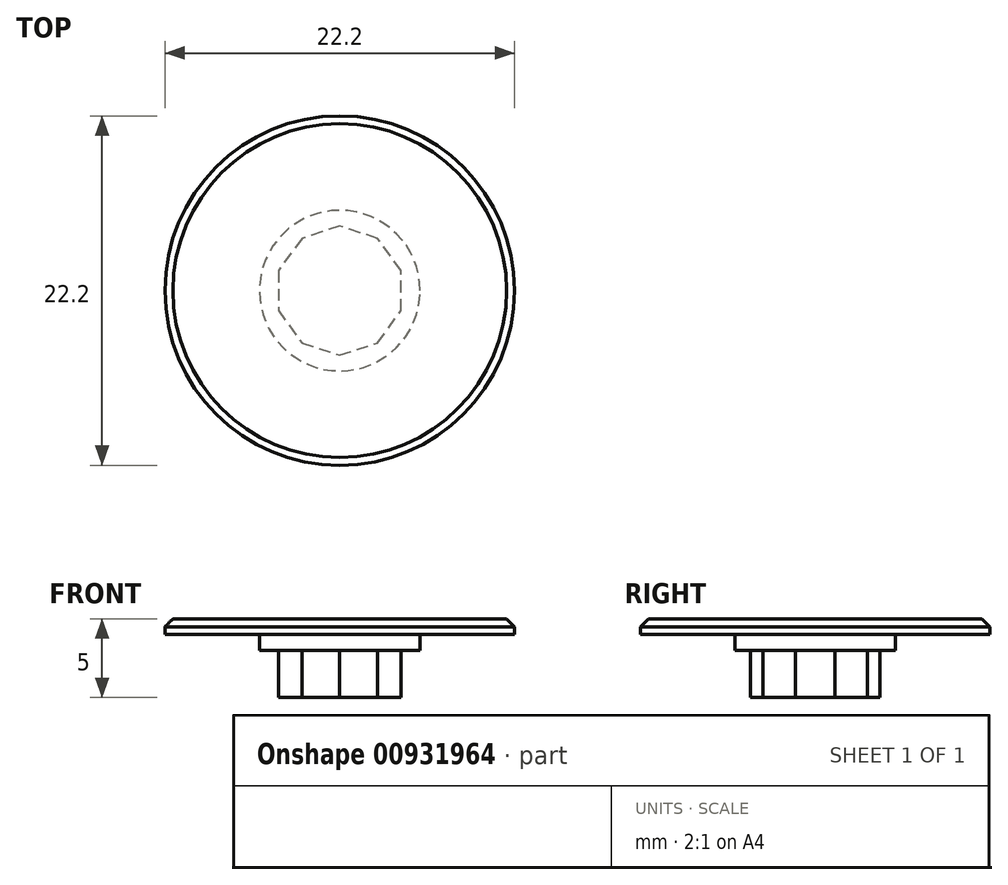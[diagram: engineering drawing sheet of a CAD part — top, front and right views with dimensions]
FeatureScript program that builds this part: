
annotation { "Feature Type Name" : "Feature", "Feature Type Description" : "" }
export const myFeature = defineFeature(function(context is Context, id is Id, definition is map)
    precondition{}
    {
        {
            var Q0;
            Q0=qCreatedBy(makeId("Front.planeOp"),FACE);
            var sketch = newSketch(context, id + "F0", { "sketchPlane" : qUnion([Q0])});
            skLineSegment(sketch, "E0", {"start": v(0, 0) * mm, "end": v(-4.1, 0) * mm});
            skLineSegment(sketch, "E1", {"start": v(-4.1, 0) * mm, "end": v(-4.1, 3) * mm});
            skLineSegment(sketch, "E2", {"start": v(-4.1, 3) * mm, "end": v(-5.1, 3) * mm});
            skLineSegment(sketch, "E3", {"start": v(0, 5) * mm, "end": v(0, 0) * mm});
            skLineSegment(sketch, "E4", {"start": v(-5.1, 3) * mm, "end": v(-5.1, 4) * mm});
            skLineSegment(sketch, "E5", {"start": v(-5.1, 4) * mm, "end": v(-11.1, 4) * mm});
            skLineSegment(sketch, "E6", {"start": v(-11.1, 4) * mm, "end": v(-11.1, 5) * mm});
            skLineSegment(sketch, "E7", {"start": v(-11.1, 5) * mm, "end": v(0, 5) * mm});
            skSolve(sketch);
        }
        {
            var Q0;
            Q0=makeQuery(id+"F0.imprint","IMPRINT",FACE,{"disambiguationData":[TD([[makeQuery(id+"F0.imprint","IMPRINT",EDGE,{"derivedFrom":sQuery(id+"F0.wireOp",EDGE,"E0")}),-1.0]])]});
            var Q1;
            Q1=sQuery(id+"F0.wireOp",EDGE,"E3");
            revolve(context, id + "F1", {"surfaceOperationType" : NewSurfaceOperationType.NEW, "entities" : qUnion([Q0]), "axis" : qUnion([Q1]), "revolveType" : RevolveType.FULL});
        }
        {
            var Q0;
            Q0=makeQuery(id+"F1.opRevolve","SWEPT_EDGE",EDGE,{"disambiguationData":[OSD([sQuery(id+"F0.wireOp",EDGE,"E6"),sQuery(id+"F0.wireOp",EDGE,"E7")])]});
            chamfer(context, id + "F2", {"entities" : qUnion([Q0]), "width" : 0.5 * mm, "tangentPropagation" : true});
        }
        {
            var Q0;
            Q0=makeQuery(id+"F1.opRevolve","SWEPT_FACE",FACE,{"disambiguationData":[OSD([sQuery(id+"F0.wireOp",EDGE,"E0")])]});
            var sketch = newSketch(context, id + "F3", { "sketchPlane" : qUnion([Q0])});
            skCircle(sketch, "E8.cCircle", {"center": v(0, 0) * mm, "radius": 4.1 * mm, "construction": true});
            skLineSegment(sketch, "E8.0", {"start": v(0, 4.1) * mm, "end": v(2.4, 3.32) * mm});
            skLineSegment(sketch, "E8.1", {"start": v(2.4, 3.32) * mm, "end": v(3.9, 1.27) * mm});
            skLineSegment(sketch, "E8.2", {"start": v(3.9, 1.27) * mm, "end": v(3.9, -1.27) * mm});
            skLineSegment(sketch, "E8.3", {"start": v(3.9, -1.27) * mm, "end": v(2.4, -3.32) * mm});
            skLineSegment(sketch, "E8.4", {"start": v(2.4, -3.32) * mm, "end": v(0, -4.1) * mm});
            skLineSegment(sketch, "E8.5", {"start": v(0, -4.1) * mm, "end": v(-2.4, -3.32) * mm});
            skLineSegment(sketch, "E8.6", {"start": v(-2.4, -3.32) * mm, "end": v(-3.9, -1.27) * mm});
            skLineSegment(sketch, "E8.7", {"start": v(-3.9, -1.27) * mm, "end": v(-3.9, 1.27) * mm});
            skLineSegment(sketch, "E8.8", {"start": v(-3.9, 1.27) * mm, "end": v(-2.4, 3.32) * mm});
            skLineSegment(sketch, "E8.9", {"start": v(-2.4, 3.32) * mm, "end": v(0, 4.1) * mm});
            skCircle(sketch, "E9.0.0", {"center": v(0, 0) * mm, "radius": 4.1 * mm});
            skSolve(sketch);
        }
        {
            var Q0;
            {var subQ0=sQuery(id+"F3.wireOp",EDGE,"E8.0");Q0=makeQuery(id+"F3.imprint","IMPRINT",FACE,{"disambiguationData":[TD([[makeQuery(id+"F3.imprint","IMPRINT",EDGE,{"derivedFrom":subQ0}),1.0]])]});}
            var Q1;
            {var subQ0=sQuery(id+"F3.wireOp",EDGE,"E8.1");Q1=makeQuery(id+"F3.imprint","IMPRINT",FACE,{"disambiguationData":[TD([[makeQuery(id+"F3.imprint","IMPRINT",EDGE,{"derivedFrom":subQ0}),1.0]])]});}
            var Q2;
            {var subQ0=sQuery(id+"F3.wireOp",EDGE,"E8.2");Q2=makeQuery(id+"F3.imprint","IMPRINT",FACE,{"disambiguationData":[TD([[makeQuery(id+"F3.imprint","IMPRINT",EDGE,{"derivedFrom":subQ0}),1.0]])]});}
            var Q3;
            {var subQ0=sQuery(id+"F3.wireOp",EDGE,"E8.3");Q3=makeQuery(id+"F3.imprint","IMPRINT",FACE,{"disambiguationData":[TD([[makeQuery(id+"F3.imprint","IMPRINT",EDGE,{"derivedFrom":subQ0}),1.0]])]});}
            var Q4;
            {var subQ0=sQuery(id+"F3.wireOp",EDGE,"E8.4");Q4=makeQuery(id+"F3.imprint","IMPRINT",FACE,{"disambiguationData":[TD([[makeQuery(id+"F3.imprint","IMPRINT",EDGE,{"derivedFrom":subQ0}),1.0]])]});}
            var Q5;
            {var subQ0=sQuery(id+"F3.wireOp",EDGE,"E8.5");Q5=makeQuery(id+"F3.imprint","IMPRINT",FACE,{"disambiguationData":[TD([[makeQuery(id+"F3.imprint","IMPRINT",EDGE,{"derivedFrom":subQ0}),1.0]])]});}
            var Q6;
            {var subQ0=sQuery(id+"F3.wireOp",EDGE,"E8.6");Q6=makeQuery(id+"F3.imprint","IMPRINT",FACE,{"disambiguationData":[TD([[makeQuery(id+"F3.imprint","IMPRINT",EDGE,{"derivedFrom":subQ0}),1.0]])]});}
            var Q7;
            {var subQ0=sQuery(id+"F3.wireOp",EDGE,"E8.7");Q7=makeQuery(id+"F3.imprint","IMPRINT",FACE,{"disambiguationData":[TD([[makeQuery(id+"F3.imprint","IMPRINT",EDGE,{"derivedFrom":subQ0}),1.0]])]});}
            var Q8;
            {var subQ0=sQuery(id+"F3.wireOp",EDGE,"E8.8");Q8=makeQuery(id+"F3.imprint","IMPRINT",FACE,{"disambiguationData":[TD([[makeQuery(id+"F3.imprint","IMPRINT",EDGE,{"derivedFrom":subQ0}),1.0]])]});}
            var Q9;
            {var subQ0=sQuery(id+"F3.wireOp",EDGE,"E8.9");Q9=makeQuery(id+"F3.imprint","IMPRINT",FACE,{"disambiguationData":[TD([[makeQuery(id+"F3.imprint","IMPRINT",EDGE,{"derivedFrom":subQ0}),1.0]])]});}
            extrude(context, id + "F4", {"entities" : qUnion([Q0, Q1, Q2, Q3, Q4, Q5, Q6, Q7, Q8, Q9]), "operationType" : NewBodyOperationType.REMOVE, "oppositeDirection" : true, "depth" : 3 * mm, "offsetDistance" : 25 * mm});
        }
    });
